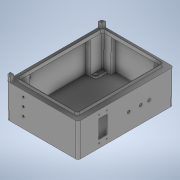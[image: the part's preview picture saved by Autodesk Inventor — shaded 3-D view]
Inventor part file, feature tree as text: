
AUTODESK INVENTOR PART (.ipt)
format: ipt  version: 2021 (Build 250183000, 183)  size: 594,432 bytes
history: native  units: mm
features: extrude x18, sketch x17, projected_geometry x17, draft x7, plane x6, hole x3, fillet x2, shell x1
ambient origin geometry x8: Origin, YZ Plane, XZ Plane, XY Plane, X Axis, Y Axis, Z Axis, Center Point
bodies: Solid1 (feature_tree)
feature tree (71):
  extrude  "Extrusion1"  Depth=398.5mm
  extrude  "Extrusion2"  Depth=139.8mm
  shell  "Shell1"  Thickness=256.0mm
  extrude  "Extrusion3"  Depth=10.0mm
  plane  "Work Plane1"
  plane  "Work Plane2"
  plane  "Work Plane3"
  plane  "Work Plane4"
  plane  "Work Plane5"
  plane  "Work Plane6"
  sketch  "Sketch4"  dims[d8=11.8mm d9=0.0mm d10=2.7mm]
  extrude  "Extrusion4"  Depth=2.7mm
  extrude  "Extrusion5"  Depth=17.0mm TaperAngle=0.0deg
  sketch  "Sketch5"  dims[d11=2.4mm d12=17.0mm d13=0.0mm]
  extrude  "Extrusion6"  Depth=247.0mm
  extrude  "Extrusion7"  Depth=14.0mm TaperAngle=0.0deg
  extrude  "Extrusion8"  Depth=14.0mm TaperAngle=0.0deg
  extrude  "Extrusion9"  Depth=351.5mm
  draft  "FaceDraft1"
  draft  "FaceDraft2"
  draft  "FaceDraft3"
  draft  "FaceDraft4"
  draft  "FaceDraft5"
  draft  "FaceDraft6"
  draft  "FaceDraft7"
  fillet  "Fillet1"  Radius=14.0mm
  extrude  "Extrusion10"  Depth=14.0mm
  extrude  "Extrusion11"  Depth=0.174533mm
  extrude  "Extrusion12"  Depth=0.174533mm
  extrude  "Extrusion13"  Depth=0.174533mm
  sketch  "Sketch13"  dims[d34=0.174533mm d35=0.174533mm]
  extrude  "Extrusion15"  Depth=20.0mm
  hole  "Hole2"  [1 undecoded]
  extrude  "Extrusion16"  Depth=15.82mm
  fillet  "Fillet2"  Radius=15.82mm
  hole  "Hole3"  [1 undecoded]
  extrude  "Extrusion17"  Depth=6.0mm
  extrude  "Extrusion18"  Depth=6.0mm
  extrude  "Extrusion20"  Depth=6.0mm
  hole  "Hole4"  [1 undecoded]
  sketch  "Sketch1"  dims[d0=298.5mm d1=398.5mm]
  sketch  "Sketch2"  dims[d2=10.0mm d3=139.8mm d4=0.053646mm d5=256.0mm]
  sketch  "Sketch3"  dims[d6=361.5mm d7=10.0mm]
  projected_geometry  "Projected Loop1"
  sketch  "Sketch6"  dims[d14=126.8mm d15=-126.8mm d16=89.5mm d17=-89.5mm d18=247.0mm]
  projected_geometry  "Projected Loop2"
  projected_geometry  "Projected Loop3"
  sketch  "Sketch7"  dims[d19=14.0mm d20=0.0mm d21=14.0mm d22=0.0mm]
  projected_geometry  "Projected Loop4"
  projected_geometry  "Projected Loop5"
  sketch  "Sketch8"  dims[d23=247.0mm d24=14.0mm d25=0.0mm]
  projected_geometry  "Projected Loop6"
  sketch  "Sketch9"  dims[d26=14.0mm d27=0.0mm d28=351.5mm d29=14.0mm d30=0.0mm]
  projected_geometry  "Projected Loop7"
  projected_geometry  "Projected Loop8"
  projected_geometry  "Projected Loop9"
  projected_geometry  "Projected Loop10"
  sketch  "Sketch11"  dims[d31=14.0mm d32=0.0mm d33=0.174533mm]
  sketch  "Sketch14"  dims[d36=0.174533mm d37=0.174533mm]
  projected_geometry  "Projected Loop11"
  sketch  "Sketch15"  dims[d38=0.174533mm d39=0.174533mm]
  sketch  "Sketch16"  dims[d40=6.0mm d41=20.0mm]
  projected_geometry  "Projected Loop12"
  sketch  "Sketch17"  dims[d43=12.0mm d44=8.2mm d45=0.0mm]
  projected_geometry  "Projected Loop13"
  sketch  "Sketch19"  dims[d46=15.82mm d47=15.82mm d48=15.82mm]
  projected_geometry  "Projected Loop14"
  projected_geometry  "Projected Loop15"
  projected_geometry  "Projected Loop16"
  projected_geometry  "Projected Loop17"
  sketch  "Sketch20"  dims[d49=15.82mm d50=227.8mm d51=227.8mm d52=275.7mm d53=275.7mm d54=113.9mm d55=113.9mm d56=137.85mm d57=137.85mm d58=8.0mm d59=0.0mm d60=7.9mm d61=7.9mm d62=7.9mm d63=7.9mm d64=7.9mm d65=0.0mm d66=245.0mm d67=289.0mm d68=211.0mm d69=259.0mm d70=2.0mm d71=0.0mm d86=32.0mm d87=103.0mm d88=70.0mm d89=85.0mm d90=35.0mm d91=76.0mm d92=10.0mm d93=0.0mm d94=4.5mm d95=6.0mm d96=9.4mm d97=2.0mm d98=90.0deg d99=8.0mm d100=20.594885mm d101=2.0mm d102=15.8mm d103=15.4mm d104=23.0mm d105=0.0mm d106=2.0mm d107=90.0mm d108=175.0mm d109=140.0mm d110=12.2mm d111=6.0mm d112=4.0mm d113=2.0mm d114=90.0deg d115=8.0mm d116=20.594885mm d117=20.0mm d118=45.0mm d119=22.0mm d127=23.0mm d128=0.0mm d129=12.0mm d130=60.0mm d131=8.2mm d132=8.2mm d133=45.0mm d134=70.0mm d135=35.0mm d136=60.0mm d137=8.2mm d138=23.0mm d139=0.0mm d148=8.2mm d149=8.2mm d150=8.2mm d151=8.2mm d152=0.0mm d153=0.0mm d154=213.0mm d155=335.0mm d156=3.0mm d157=6.0mm d158=4.0mm d159=2.0mm d160=90.0deg d161=6.0mm d162=20.594885mm]
note: 3 required parameter values undecoded (feature->parameter linkage not recoverable at this tier; creation-order binding heuristic only, values carry confidence <= 0.55)
